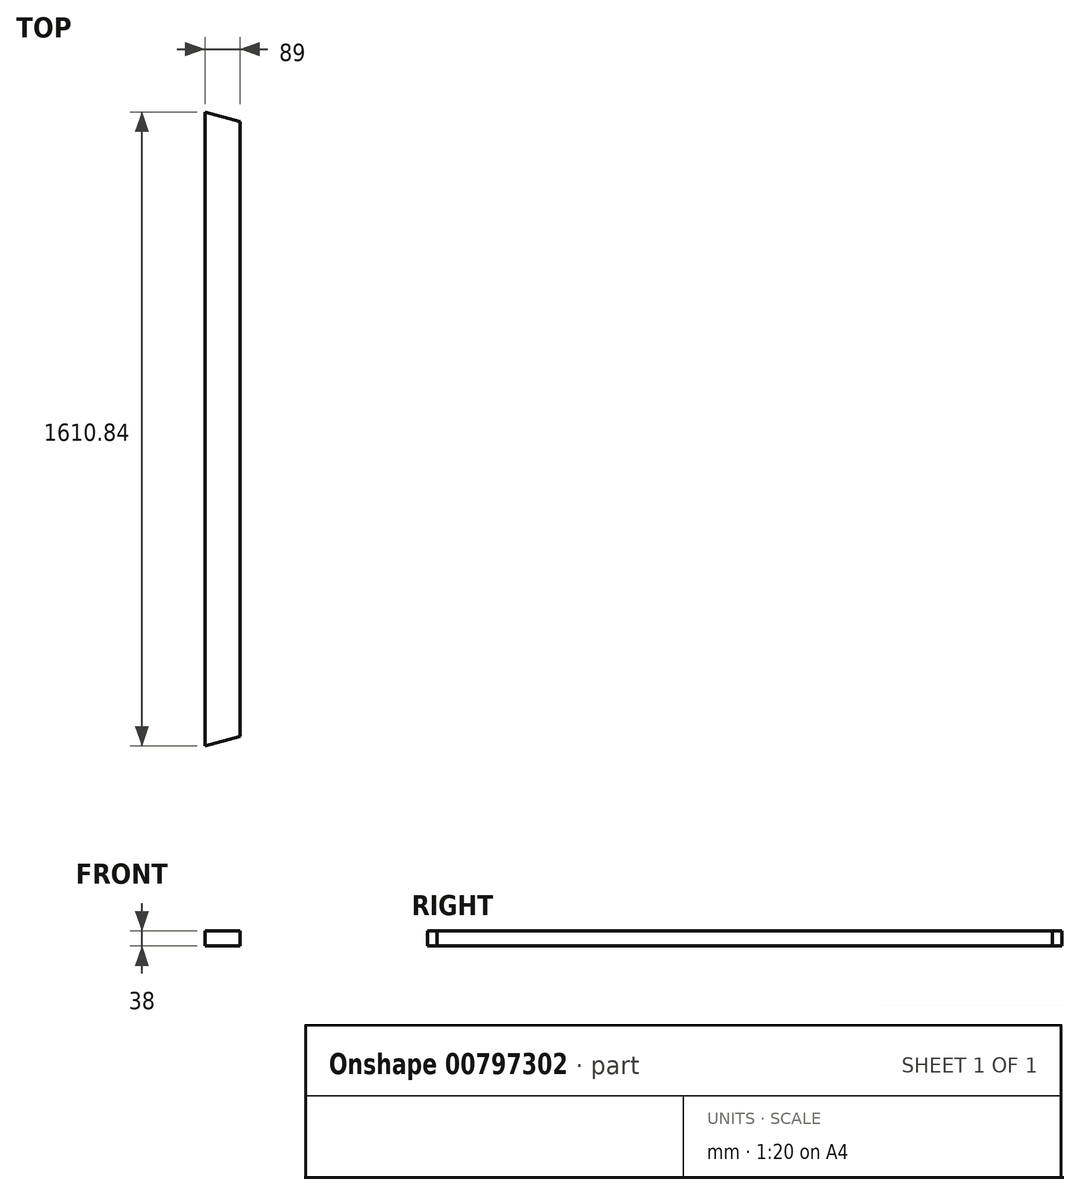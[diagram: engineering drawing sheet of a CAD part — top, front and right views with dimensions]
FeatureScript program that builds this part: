
annotation { "Feature Type Name" : "Feature", "Feature Type Description" : "" }
export const myFeature = defineFeature(function(context is Context, id is Id, definition is map)
    precondition{}
    {
        {
            var Q0;
            Q0=qCreatedBy(makeId("Front.planeOp"),FACE);
            var sketch = newSketch(context, id + "F0", { "sketchPlane" : qUnion([Q0])});
            skLineSegment(sketch, "E0.bottom", {"start": v(44.5, 19) * mm, "end": v(-44.5, 19) * mm});
            skLineSegment(sketch, "E0.top", {"start": v(44.5, -19) * mm, "end": v(-44.5, -19) * mm});
            skLineSegment(sketch, "E0.left", {"start": v(44.5, 19) * mm, "end": v(44.5, -19) * mm});
            skLineSegment(sketch, "E0.right", {"start": v(-44.5, 19) * mm, "end": v(-44.5, -19) * mm});
            skPoint(sketch, "E0.middle", {"position": v(0, 0) * mm});
            skSolve(sketch);
        }
        {
            var Q0;
            Q0=qSketchRegion(id+"F0",true);
            extrude(context, id + "F1", {"entities" : qUnion([Q0]), "depth" : (1285.08 + 325.76) * mm, "offsetDistance" : 25 * mm, "symmetric" : true});
        }
        {
            var Q0;
            Q0=makeQuery(id+"F1.opExtrude","SWEPT_FACE",FACE,{"disambiguationData":[OSD([sQuery(id+"F0.wireOp",EDGE,"E0.bottom")])]});
            var sketch = newSketch(context, id + "F2", { "sketchPlane" : qUnion([Q0])});
            skLineSegment(sketch, "E1", {"start": v(-44.5, -805.42) * mm, "end": v(44.5, -781.57) * mm});
            skLineSegment(sketch, "E2", {"start": v(44.5, -781.57) * mm, "end": v(44.5, -805.42) * mm});
            skLineSegment(sketch, "E3", {"start": v(44.5, -805.42) * mm, "end": v(-44.5, -805.42) * mm});
            skLineSegment(sketch, "E4", {"start": v(-44.5, 805.42) * mm, "end": v(44.5, 781.57) * mm});
            skLineSegment(sketch, "E5", {"start": v(44.5, 781.57) * mm, "end": v(44.5, 805.42) * mm});
            skLineSegment(sketch, "E6", {"start": v(44.5, 805.42) * mm, "end": v(-44.5, 805.42) * mm});
            skSolve(sketch);
        }
        {
            var Q0;
            Q0 = qSketchRegion(id + "F2", true);
            extrude(context, id + "F3", {"entities" : qUnion([Q0]), "operationType" : NewBodyOperationType.REMOVE, "endBound" : BoundingType.THROUGH_ALL, "oppositeDirection" : true, "depth" : 25 * mm, "offsetDistance" : 25 * mm});
        }
    });
